# Revit family: Toilet_Seat-Elongated_Closed_Front-KOHLER-Avantis-K-4761_1
name_source: partatom
category: Specialty Equipment
revit_build: Autodesk Revit 2015 (Build: 20140606_1530(x64)
units: mm (PartAtom-declared; Revit-internal decimal feet)

## types (4) — shared parameters
ADA Compliant = No
Assembly Code = C1030200
Date Modified = 06/03/2019
Default Elevation = 0"
Height = 13/16"
Length = 18 1/16"
Manufacturer = KOHLER Co.
MasterFormat 1995 = 10820
MasterFormat 2004 = 10.28.13
Material = Solid Wood
Product Documentation Link = https://www.us.kohler.com
Product Name = Avantis
Product Page URL = http://www.us.kohler.com
URL = https://www.us.kohler.com
WaterSense Certified = No
Width = 14 3/16"

## per-type parameters (varying)
| type | Description | Finish | Hinge Finish | Model | Type |
| Vibrant Brushed Nickel Hinges-BN,LAW-Light Antique Walnut | Elongated toilet seat with Quick-Release Vibrant Brushed Nickel metal hinges | Kohler-Wood-LAW-Light_Antique_Walnut | Kohler-Metal-BN-Vibrant_Brushed_Nickel | K-4761-BN-LAW | 1 |
| Vibrant Brushed Nickel Hinges-BN,DAW-Dark Antique Walnut | Elongated toilet seat with Quick-Release Vibrant Brushed Nickel metal hinges | Kohler-Wood-DAW-Dark_Antique_Walnut | Kohler-Metal-BN-Vibrant_Brushed_Nickel | K-4761-BN-DAW | 2 |
| Polished Chrome Hinges-CP,LAW-Light Antique Walnut | Elongated toilet seat with Quick-Release Polished Chrome metal hinges | Kohler-Wood-LAW-Light_Antique_Walnut | Kohler-Metal-CP-Polished_Chrome | K-4761-CP-LAW | 3 |
| Polished Chrome Hinges-CP,DAW-Dark Antique Walnut | Elongated toilet seat with Quick-Release Polished Chrome metal hinges | Kohler-Wood-DAW-Dark_Antique_Walnut | Kohler-Metal-CP-Polished_Chrome | K-4761-CP-DAW | 4 |

## geometry (parser evidence)
native form markers: Sweep x4
no freeform markers — native parametric forms only
